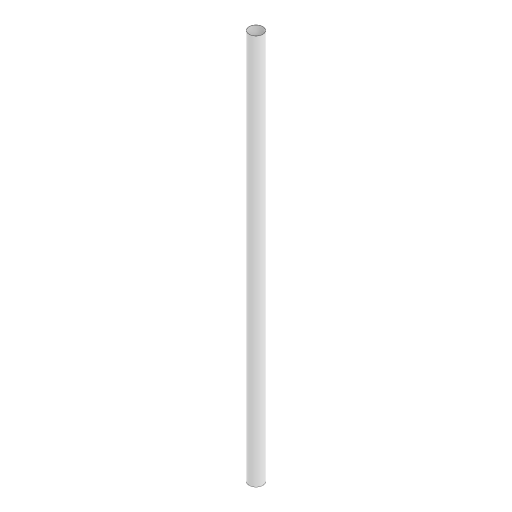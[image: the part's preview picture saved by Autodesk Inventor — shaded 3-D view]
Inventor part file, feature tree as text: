
AUTODESK INVENTOR PART (.ipt)
format: ipt  version: 2024.3 (Build 283343000, 343)  size: 83,456 bytes
history: native  units: mm
features: extrude x1, sketch x1
ambient origin geometry x8: Origin, YZ Plane, XZ Plane, XY Plane, X Axis, Y Axis, Z Axis, Center Point
bodies: Solid1 (feature_tree)
feature tree (2):
  extrude  "Extrusion1"  Depth=120.0mm
  sketch  "Sketch1"  dims[d0=4.1mm d1=4.2mm d2=120.0mm d3=0.0mm]
